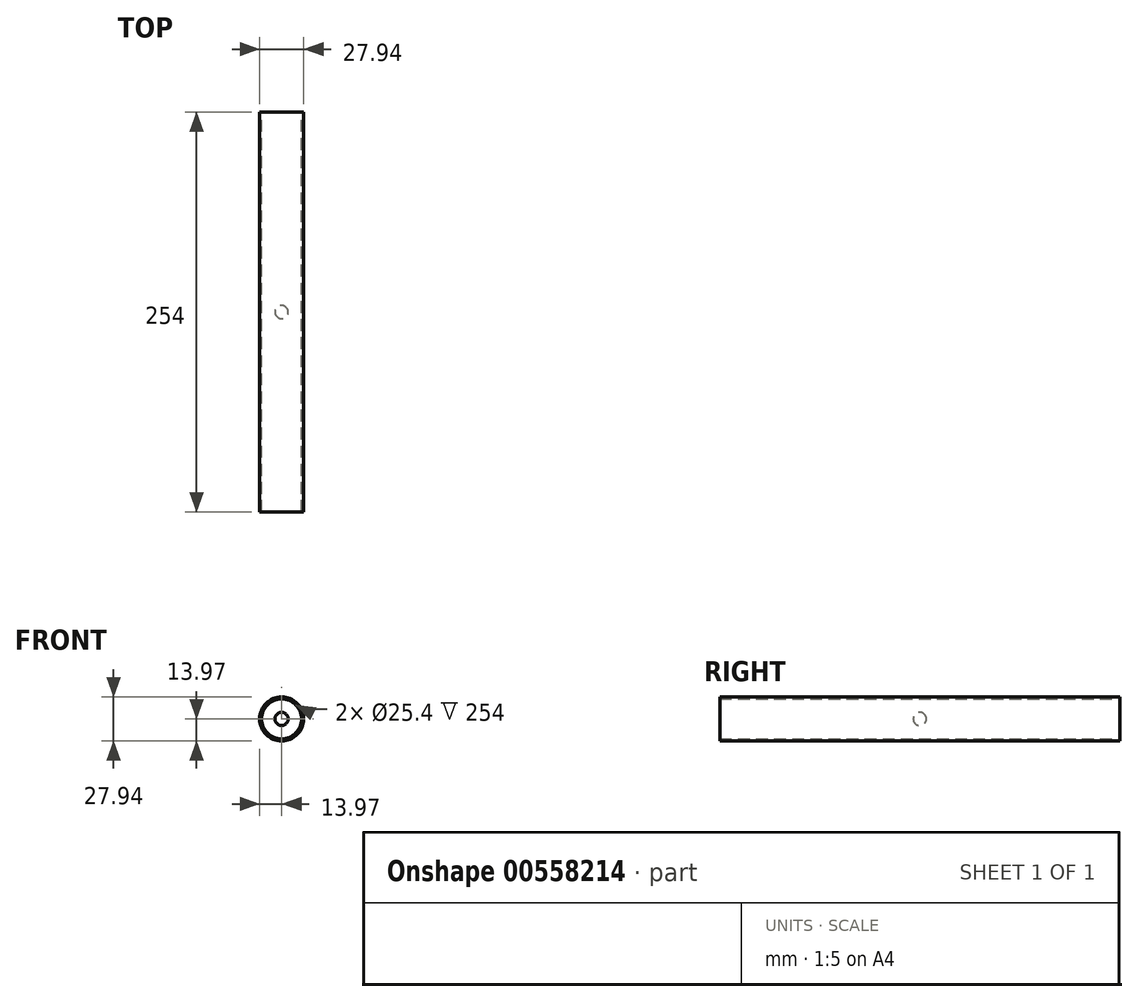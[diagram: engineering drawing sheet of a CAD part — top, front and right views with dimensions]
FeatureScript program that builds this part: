
annotation { "Feature Type Name" : "Feature", "Feature Type Description" : "" }
export const myFeature = defineFeature(function(context is Context, id is Id, definition is map)
    precondition{}
    {
        {
            var Q0;
            Q0=qCreatedBy(makeId("Front.planeOp"),FACE);
            var sketch = newSketch(context, id + "F0", { "sketchPlane" : qUnion([Q0])});
            skCircle(sketch, "E0", {"center": v(0, 0) * mm, "radius": 13.97 * mm});
            skCircle(sketch, "E1", {"center": v(0, 0) * mm, "radius": 12.7 * mm});
            skArc(sketch, "E2", {"start": v(4.2, 0) * mm, "mid": v(0, 4.2) * mm, "end": v(-4.2, 0) * mm});
            skLineSegment(sketch, "E3", {"start": v(-4.2, 0) * mm, "end": v(4.2, 0) * mm});
            skSolve(sketch);
        }
        {
            var Q0;
            Q0=makeQuery(id+"F0.imprint","IMPRINT",FACE,{"disambiguationData":[TD([[makeQuery(id+"F0.imprint","IMPRINT",EDGE,{"derivedFrom":sQuery(id+"F0.wireOp",EDGE,"E2")}),1.0]])]});
            var Q1;
            Q1=sQuery(id+"F0.wireOp",EDGE,"E3");
            revolve(context, id + "F1", {"entities" : qUnion([Q0]), "axis" : qUnion([Q1]), "revolveType" : RevolveType.FULL});
        }
        {
            var Q0;
            Q0=makeQuery(id+"F0.imprint","IMPRINT",FACE,{"disambiguationData":[TD([[makeQuery(id+"F0.imprint","IMPRINT",EDGE,{"derivedFrom":sQuery(id+"F0.wireOp",EDGE,"E0")}),1.0]])]});
            extrude(context, id + "F2", {"entities" : qUnion([Q0]), "endBound" : BoundingType.SYMMETRIC, "depth" : 254 * mm, "offsetDistance" : 25.4 * mm});
        }
    });
